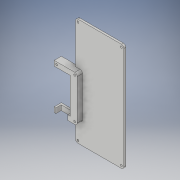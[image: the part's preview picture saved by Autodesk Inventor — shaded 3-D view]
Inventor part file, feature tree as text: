
AUTODESK INVENTOR PART (.ipt)
format: ipt  version: 2019 (Build 230136000, 136)  size: 179,712 bytes
history: native  units: in
note: dims shown in document units (in); Inventor stores cm internally (conversion verified against a paired STEP export)
features: sketch x4, extrude x2, hole x2, other x1
ambient origin geometry x8: Origin, YZ Plane, XZ Plane, XY Plane, X Axis, Y Axis, Z Axis, Center Point
bodies: Solid1 (feature_tree)
feature tree (9):
  other  "PhoneCover"
  extrude  "Phone Cover"  Depth=2.13in
  hole  "Phone Holes"  [1 undecoded]
  extrude  "Scanner Wall"  Depth=0.125in
  hole  "Scanner Holes"  [1 undecoded]
  sketch  "Sketch1"  dims[d0=2.43in d1=2.13in]
  sketch  "Sketch2"  dims[d4=1.0in d5=0.1in d6=0.0in]
  sketch  "Sketch3"  dims[d7=0.125in d8=0.125in]
  sketch  "Sketch4"  dims[d9=0.125in d10=0.125in d11=0.1in d12=0.75in d13=0.375in d14=0.25in d15=0.5635in d16=1.0in d17=0.8108in d22=0.81in d23=0.25in d24=0.25in d25=0.09in d26=0.125in d27=0.26in d28=0.0in d29=0.125in d30=0.125in d32=0.125in d33=0.35in d34=0.1in d35=0.75in d36=0.375in d37=0.25in d38=0.5635in d39=0.18in d40=0.8108in d41=0.125in d42=5.4in d43=0.125in d44=0.125in d45=0.125in d46=0.125in d48=0.125in d49=0.125in d50=0.125in d51=0.125in]
note: 2 required parameter values undecoded (feature->parameter linkage not recoverable at this tier; creation-order binding heuristic only, values carry confidence <= 0.55)
